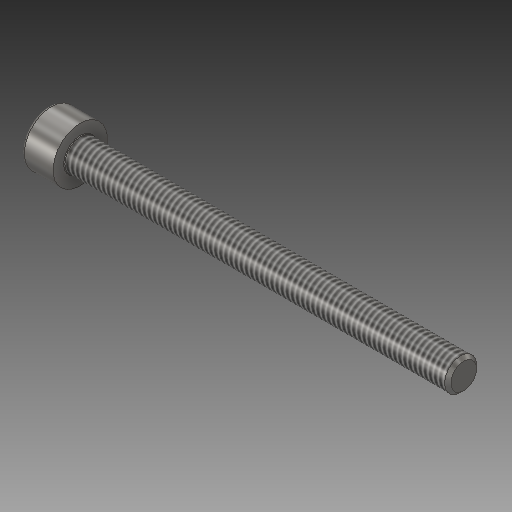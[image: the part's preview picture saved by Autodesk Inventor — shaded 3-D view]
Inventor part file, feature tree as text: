
AUTODESK INVENTOR PART (.ipt)
format: ipt  version: 2017 (Build 210142000, 142)  size: 194,048 bytes
history: native  units: mm
features: other x6, sketch x2, plane x1
ambient origin geometry x8: Origin, YZ Plane, XZ Plane, XY Plane, X Axis, Y Axis, Z Axis, Center Point
bodies: Solid1 (feature_tree)
feature tree (9):
  other  "Forged Socket Head Cap Screw - Metric M5x0.8 x 60"
  other  "Solid1::Forged Socket Head Cap Screw - Metric M5x0.8 x 60"
  other  "TaggingFeature1"
  sketch  "Sketch1"  dims[d0=10.0mm]
  sketch  "Sketch2"  dims[d19=0.0mm d28=0.0mm d29=0.0mm]
  plane  "Work Plane1"
  other  "Align 2D"
  other  "Align1"
  other  "Insert In1"
